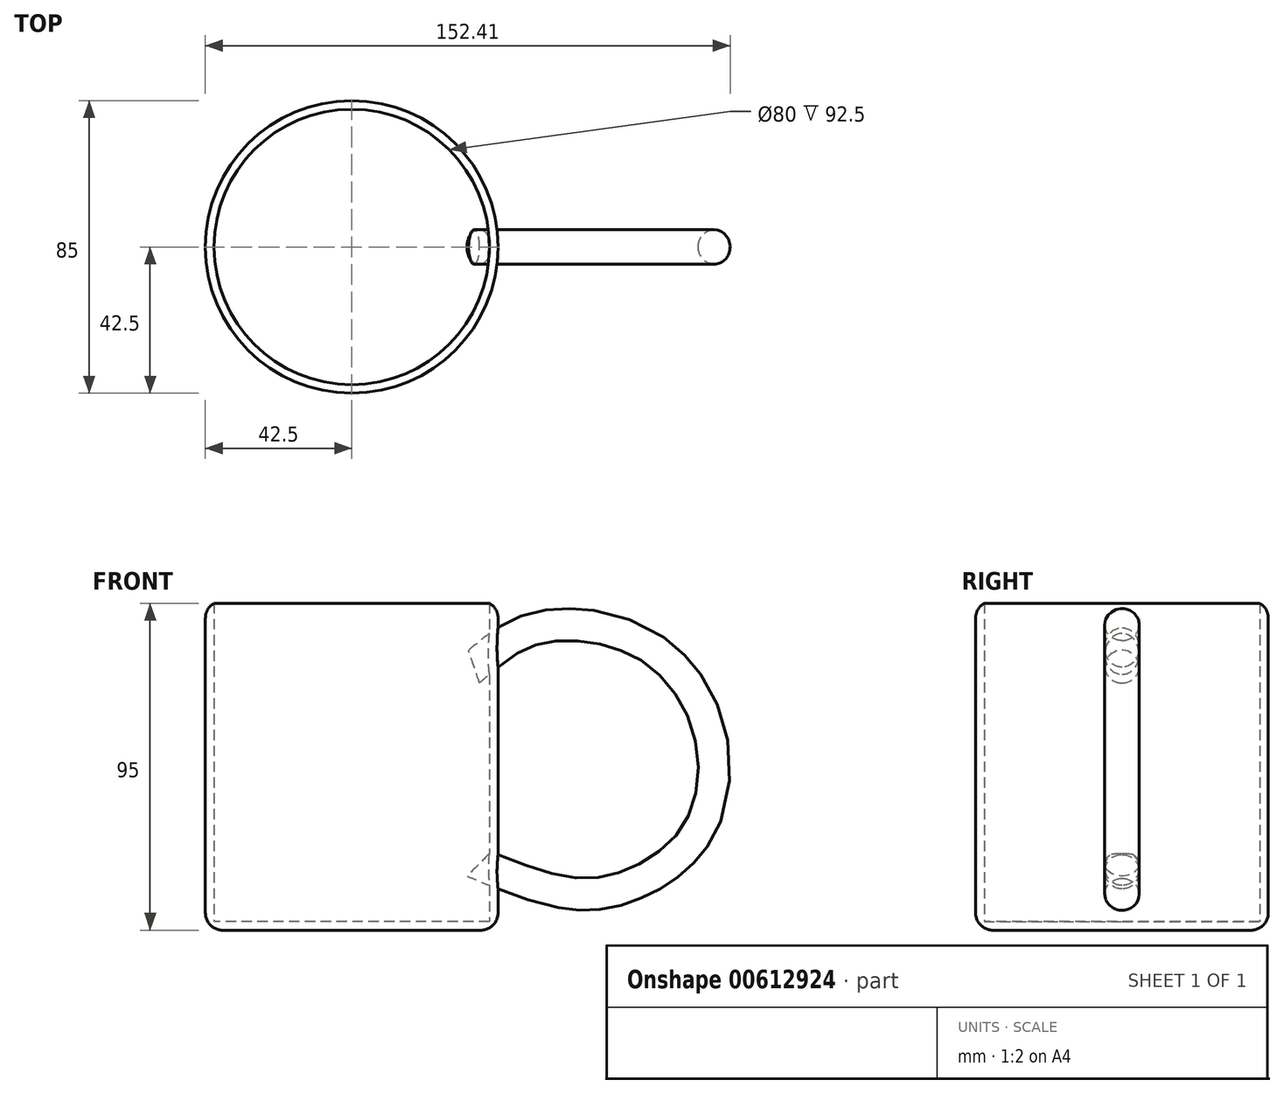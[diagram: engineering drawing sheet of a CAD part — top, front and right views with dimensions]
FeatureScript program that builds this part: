
annotation { "Feature Type Name" : "Feature", "Feature Type Description" : "" }
export const myFeature = defineFeature(function(context is Context, id is Id, definition is map)
    precondition{}
    {
        {
            var Q0;
            Q0=qCreatedBy(makeId("Top.planeOp"),FACE);
            var sketch = newSketch(context, id + "F0", { "sketchPlane" : qUnion([Q0])});
            skCircle(sketch, "E0", {"center": v(0, 0) * mm, "radius": 42.5 * mm});
            skSolve(sketch);
        }
        {
            var Q0;
            Q0=makeQuery(id+"F0.imprint","IMPRINT",FACE,{"disambiguationData":[TD([[makeQuery(id+"F0.imprint","IMPRINT",EDGE,{"derivedFrom":sQuery(id+"F0.wireOp",EDGE,"E0")}),1.0]])]});
            extrude(context, id + "F1", {"entities" : qUnion([Q0]), "depth" : 100 * mm, "offsetDistance" : 25 * mm});
        }
        {
            var Q0;
            Q0=makeQuery(id+"F1.opExtrude","CAP_FACE",FACE,{"disambiguationData":[OSD([sQuery(id+"F0.wireOp",EDGE,"E0")])],"isStart":false});
            shell(context, id + "F2", {"entities" : qUnion([Q0]), "thickness" : 2.5 * mm});
        }
        {
            var Q0;
            Q0=qCreatedBy(makeId("Front.planeOp"),FACE);
            var sketch = newSketch(context, id + "F3", { "sketchPlane" : qUnion([Q0])});
            skFitSpline(sketch, "E1", {"points": [v(35.63, 76.31) * mm, v(50.42, 86.44) * mm, v(69.5, 88) * mm, v(88.97, 80.2) * mm, v(103.37, 58.8) * mm, v(101.43, 30.76) * mm, v(84.3, 14.8) * mm, v(64.05, 10.9) * mm, v(37.18, 19.47) * mm], "startDerivative": vector(125.2, 107.99) * mm, "endDerivative": vector(-199.29, 83.42) * mm});
            skSolve(sketch);
        }
        {
            var Q0;
            Q0=qCreatedBy(makeId("Right.planeOp"),FACE);
            cPlane(context, id + "F4", {"entities" : qUnion([Q0]), "cplaneType" : CPlaneType.OFFSET, "offset" : 50 * mm, "width" : 150 * mm, "height" : 150 * mm});
        }
        {
            var Q0;
            Q0=qCreatedBy(id+"F4.planeOp",FACE);
            var sketch = newSketch(context, id + "F5", { "sketchPlane" : qUnion([Q0])});
            skCircle(sketch, "E2", {"center": v(0, 86.55) * mm, "radius": 5 * mm});
            skSolve(sketch);
        }
        {
            var Q0;
            Q0=makeQuery(id+"F5.imprint","IMPRINT",FACE,{"disambiguationData":[TD([[makeQuery(id+"F5.imprint","IMPRINT",EDGE,{"derivedFrom":sQuery(id+"F5.wireOp",EDGE,"E2")}),1.0]])]});
            var Q1;
            Q1=sQuery(id+"F3.wireOp",EDGE,"E1");
            sweep(context, id + "F6", {"operationType" : NewBodyOperationType.ADD, "profiles" : qUnion([Q0]), "path" : qUnion([Q1])});
        }
        {
            var Q0;
            Q0=makeQuery(id+"F1.opExtrude","CAP_FACE",FACE,{"disambiguationData":[OSD([sQuery(id+"F0.wireOp",EDGE,"E0")])],"isStart":true});
            fillet(context, id + "F7", {"entities" : qUnion([Q0]), "radius" : 5 * mm, "tangentPropagation" : true, "allowEdgeOverflow" : false});
        }
        {
            var Q0;
            {var subQ0=sQuery(id+"F0.wireOp",EDGE,"E0");Q0=makeQuery(id+"F2.opShell","OFFSET_EDGE",EDGE,{"disambiguationData":[OSD([subQ0]),TDD([makeQuery(id+"F1.opExtrude","CAP_EDGE",EDGE,{"disambiguationData":[OSD([subQ0])],"isStart":false})])]});}
            chamfer(context, id + "F8", {"entities" : qUnion([Q0]), "width" : 5 * mm, "tangentPropagation" : true});
        }
        {
            var Q0;
            {var subQ0=sQuery(id+"F0.wireOp",EDGE,"E0");Q0=makeQuery(id+"F8.opChamfer","BLEND_EDGE",EDGE,{"blendedFrom":[makeQuery(id+"F2.opShell","OFFSET_EDGE",EDGE,{"disambiguationData":[OSD([subQ0]),TDD([makeQuery(id+"F1.opExtrude","CAP_EDGE",EDGE,{"disambiguationData":[OSD([subQ0])],"isStart":false})])]}),makeQuery(id+"F1.opExtrude","SWEPT_FACE",FACE,{"disambiguationData":[OSD([subQ0])]})],"blendedInto":[makeQuery(id+"F1.opExtrude","SWEPT_FACE",FACE,{"disambiguationData":[OSD([subQ0])]})]});}
            fillet(context, id + "F9", {"entities" : qUnion([Q0]), "radius" : 5 * mm, "tangentPropagation" : true, "allowEdgeOverflow" : false});
        }
    });
